# Revit family: Супремус S
name_source: partatom
category: Осветительные приборы
units: mm (PartAtom-declared; Revit-internal decimal feet)

## family parameters
Всегда вертикально = Да
Источник света = Да
На основе рабочей плоскости = Нет
Общий = Нет
При загрузке вырезать с полостями = Нет
Размер круглого соединителя = Использовать диаметр
Тип детали = Нормальный
Точка расчета площади = Нет

## types (9) — shared parameters
ADSK_URL страницы изделия = https://www.allfresco.ru
ADSK_Единица измерения = шт.
ADSK_Завод-изготовитель = ALFRESCO
ADSK_Количество фаз = 2
ADSK_Модель = Супремус S ДТУ-67-AF
ADSK_Напряжение = 220 В
ADSK_Полная мощность = 0 В·А
ADSK_Ток = 0 А
ADSK_Энергоэффективность = 110 лм/Вт
Angle_загиб = 45.00°
H_дверка = 505 мм
H_конечной точки = 1500 мм
H_рассеиватель = 858 мм
IP Class = IP 67
L_ассеиватель = 223 мм
L_отступ до конечной точки = 1500 мм
L_отступ до центра = 1000 мм
R_загиба = 360 мм
S_дверка = 88 мм
S_профиль_половина = 51 мм
S_рассеиватель = 90 мм
S_точки освещения = 500 мм
S_фланец = 240 мм
h_дверка = 350 мм
h_фланец = 10 мм
x1_загиба = 103 мм
x1_рассеиватель = 50 мм
Блок аварийного питания = Нет
Класс защиты = 1
Класс пожароопасности = F (светильники предназначены для установки непосредственно на поверхность из нормально воспламеняемых материалов)
Климатическая зона = УХЛ1
Короб_Диаметр = 20 мм
Корпус светильника = Сталь, окрашенная, темно-серая
Материал рассеивателя = Светотехнический ПК
Область использования = Парки, скверы, общественные пространства, городская инфраструктура
Полная установленная мощность = 0 В·А
Рассеиватель = Белый_Светодиод
Светофильтр = 16777215
Смещение цветовой температуры при затухании лампы = <Нет>
Таблица выбора = Таблица параметров светильников_par4_v1
Температура эксплуатации = -40 +50
Тип ИС = LED-модуль
Тип КСС = тип ШБ (широкая боковая)
Тип ПРА = -
Тип продукции = LED-светильник
Угол наклона = 90.00°
Цветоывая температура = 2700-5500
zero-valued in all types: ADSK_Количество фаз числовое, ADSK_Коэффициент мощности

## per-type parameters (varying)
| type | 1 | 2 | 3 | ADSK_Артикул | ADSK_Масса | ADSK_Масса_Текст | ADSK_Наименование | ADSK_Номинальная мощность | ADSK_Размер_Высота | ADSK_Фактическая мощность | H_столб | H_точки освещения | Файл фотометрической сетки |
| ДТУ2v671 Светодиодный светильник Супремус S ДТУ-67-AF-ДТУП671(40Вт)-4,0 | Да | Нет | Нет | ДТУ2v671 | 48 | 48 | ДТУ2v671 Светодиодный светильник Супремус S ДТУ-67-AF-ДТУП671(40Вт)-4.0 | 40 Вт | 4000 мм | 39 Вт | 3000 мм | 3600 мм | DTU-68-AF Supremus S 40W 60°x130°.ies |
| ДТУ2v672 Светодиодный светильник Супремус S ДТУ-67-AF-ДТУП671(40Вт)+ДТУП671(40Вт)-4,0 | Да | Да | Нет | ДТУ2v672 | 58 | 58 | ДТУ2v672 Светодиодный светильник Супремус S ДТУ-67-AF-ДТУП671(40Вт)+ДТУП671(40Вт)-4.0 | 80 Вт | 4000 мм | 78 Вт | 3000 мм | 3600 мм | DTU-68-AF Supremus S 40W 60°x130°.ies |
| ДТУ2v6728 Светодиодный светильник Супремус S ДТУ-67-AF-ДТУП671(40Вт)_ДТУП671(40Вт)-4,0 | Нет | Да | Да | ДТУ2v6728 | 58 | 58 | ДТУ2v6728 Светодиодный светильник Супремус S ДТУ-67-AF-ДТУП671(40Вт)_ДТУП671(40Вт)-4.0 | 80 Вт | 4000 мм | 78 Вт | 3000 мм | 3600 мм | DTU-68-AF Supremus S 40W 60°x130°.ies |
| ДТУ2v673 Светодиодный светильник Супремус S ДТУ-67-AF-ДТУП671(40Вт)-5,0 | Да | Нет | Нет | ДТУ2v673 | 56 | 56 | ДТУ2v673 Светодиодный светильник Супремус S ДТУ-67-AF-ДТУП671(40Вт)-5.0 | 40 Вт | 5000 мм | 39 Вт | 4000 мм | 4600 мм | DTU-68-AF Supremus S 40W 60°x130°.ies |
| ДТУ2v675 Светодиодный светильник Супремус S ДТУ-67-AF-ДТУП671(40Вт)+ДТУП671(40Вт)-5,0 | Да | Да | Нет | ДТУ2v675 | 67 | 67 | ДТУ2v675 Светодиодный светильник Супремус S ДТУ-67-AF-ДТУП671(40Вт)+ДТУП671(40Вт)-5.0 | 80 Вт | 5000 мм | 78 Вт | 4000 мм | 4600 мм | DTU-68-AF Supremus S 40W 60°x130°.ies |
| ДТУ2v676 Светодиодный светильник Супремус S ДТУ-67-AF-ДТУП671(40Вт)_ДТУП671(40Вт)-5,0 | Нет | Да | Да | ДТУ2v676 | 67 | 67 | ДТУ2v676 Светодиодный светильник Супремус S ДТУ-67-AF-ДТУП671(40Вт)_ДТУП671(40Вт)-5.0 | 80 Вт | 5000 мм | 78 Вт | 4000 мм | 4600 мм | DTU-68-AF Supremus S 40W 60°x130°.ies |
| ДТУ2v6717 Светодиодный светильник Супремус S ДТУ-67-AF-ДТУП672(60Вт)-6,0 | Да | Нет | Нет | ДТУ2v6717 | 65 | 65 | ДТУ2v6717 Светодиодный светильник Супремус S ДТУ-67-AF-ДТУП672(60Вт)-6.0 | 60 Вт | 6000 мм | 60 Вт | 5000 мм | 5600 мм | DTU-68-AF Supremus S 60W 60°x130°.ies |
| ДТУ2v6719 Светодиодный светильник Супремус S ДТУ-67-AF-ДТУП672(60Вт)+ДТУП672(60Вт)-6,0 | Да | Да | Нет | ДТУ2v6719 | 75 | 75 | ДТУ2v6719 Светодиодный светильник Супремус S ДТУ-67-AF-ДТУП672(60Вт)+ДТУП672(60Вт)-6.0 | 120 Вт | 6000 мм | 119 Вт | 5000 мм | 5600 мм | DTU-68-AF Supremus S 60W 60°x130°.ies |
| ДТУ2v6721 Светодиодный светильник Супремус S ДТУ-67-AF-ДТУП672(60Вт)_ДТУП672(60Вт)-6,0 | Нет | Да | Да | ДТУ2v6721 | 75 | 75 | ДТУ2v6721 Светодиодный светильник Супремус S ДТУ-67-AF-ДТУП672(60Вт)_ДТУП672(60Вт)-6.0 | 120 Вт | 6000 мм | 119 Вт | 5000 мм | 5600 мм | DTU-68-AF Supremus S 60W 60°x130°.ies |

## geometry (parser evidence)
native form markers: Blend x2
no freeform markers — native parametric forms only
